# Revit family: Haworth_BeHold_Modular_AttachedCredenza_StorageCenter
name_source: partatom
category: Furniture Systems
revit_build: Autodesk Revit 2018 (Build: 20170223_1515(x64)
units: mm (PartAtom-declared; Revit-internal decimal feet)

## family parameters
Always vertical = Yes
Cut with Voids When Loaded = No
OmniClass Number = 23.40.70.14.64.21
OmniClass Title = Systems Furniture
Part Type = Normal
Room Calculation Point = No
Round Connector Dimension = Use Diameter
Shared = No
Work Plane-Based = No

## types (6) — shared parameters
Actual D/T Leg Control = No
Actual Storage Width = 36"
Actual Width = 72"
Assembly Code = E2020200
Blade Pull = Yes
Blade Pull Length = 35 13/16"
Case Thickness = 3/4"
Classic Pull = No
Classic Pull Length = 6 3/4"
Cresent Pull = No
Custom Size = No
Description = Haworth - Be_Hold - Modular Credenza - Storage Center
Distance Between Drawer = 1/8"
Double Unit Leg = No
Drawer Width = 35 7/8"
Glide Finish = Haworth _ Polymer _ Slate
Linear Pull = No
Linear Pull Length = 8"
Manufacturer = Haworth
Max. Depth = 24"
Max. Height = 22"
Max. Storage Width = 36"
Max. Width = 72"
Min. Depth = 16"
Min. Height = 22"
Min. Storage Width = 36"
Min. Width = 72"
Model = Haworth Be_Hold
Revision Number = 1
Single Unit Leg = Yes
Size = Verify Final Dim. w/ Haworth
Standard Depths = 16, 24 in.
Sustainability Info = https://www.haworth.com
Top Case Front Offset = 3"
Top Thickness = 3/4"
Triple Unit Leg = No
URL = www.haworth.com
URL - Product = https://www.haworth.com
Warranty = http://www.haworth.com
Wing Pull = No
Wing Pull Length = 16 3/4"
With Lock = Yes

## per-type parameters (varying)
| type | 16 Deep Leg | Actual Depth | Actual Height | Actual Single Leg Control | Back Case Back Control | Back Case Side Control | Bottom Case Offset | Bottom Drawer Height | Bottom Drawer Offset | Depth | Glide Control | Inset Style | Proud Style | Shelf 1 Offset | Side Case Back Control | Top Case Back Control | Top Drawer Height | Total Drawer Height | With Leg |
| 24d - Proud Back | No | 24" | 22" | No | 0" | 0" | 1/2" | 13 149/256" | 1 3/8" | 24" | Yes | No | Yes | 13 197/256" | 3/4" | 0" | 6 203/256" | 20 1/2" | No |
| 16d - Proud Back | Yes | 16" | 22" | No | 0" | 0" | 1/2" | 13 149/256" | 1 3/8" | 16" | Yes | No | Yes | 13 197/256" | 3/4" | 0" | 6 203/256" | 20 1/2" | No |
| 24d - Inset Back | No | 24" | 22" | No | 3/16" | 3/4" | 1/2" | 13 149/256" | 1 3/8" | 24" | Yes | Yes | No | 13 197/256" | 0" | 3/16" | 6 203/256" | 20 1/2" | No |
| 16d - Inset Back | Yes | 16" | 22" | No | 3/16" | 3/4" | 1/2" | 13 149/256" | 1 3/8" | 16" | Yes | Yes | No | 13 197/256" | 0" | 3/16" | 6 203/256" | 20 1/2" | No |
| 24d - Inset Back - With Leg | No | 24" | 28" | Yes | 3/16" | 3/4" | 6" | 13 235/256" | 6 7/8" | 24" | No | Yes | No | 14 27/256" | 0" | 3/16" | 6 245/256" | 21" | Yes |
| 24d - Proud Back - With Leg | No | 24" | 28" | Yes | 0" | 0" | 6" | 13 235/256" | 6 7/8" | 24" | No | No | Yes | 14 27/256" | 3/4" | 0" | 6 245/256" | 21" | Yes |

## geometry (parser evidence)
native form markers: Sweep x10
no freeform markers — native parametric forms only
